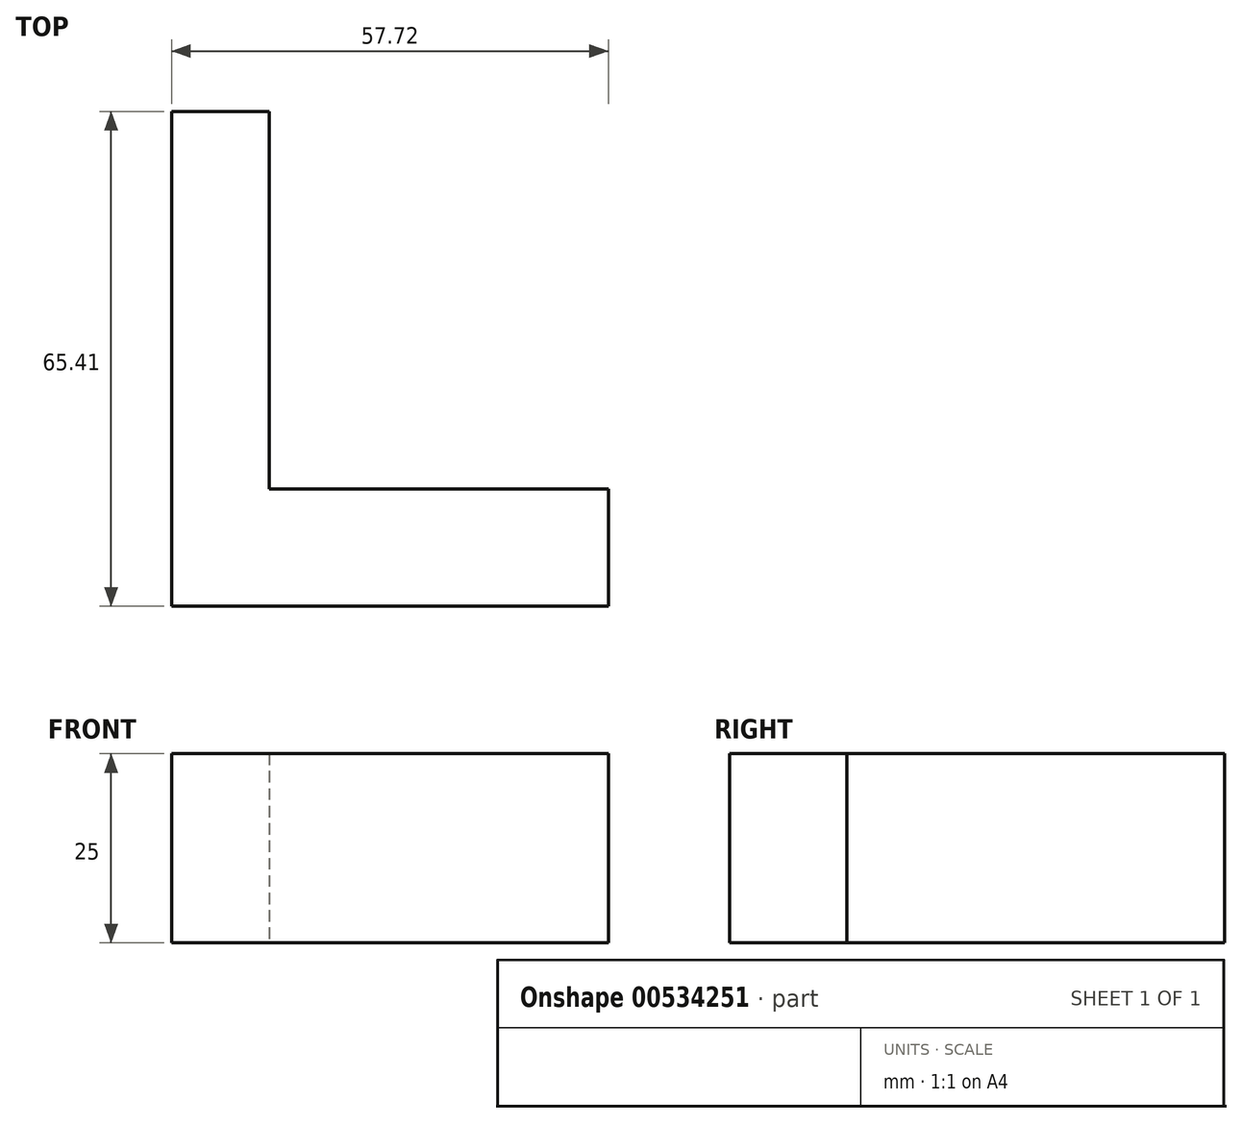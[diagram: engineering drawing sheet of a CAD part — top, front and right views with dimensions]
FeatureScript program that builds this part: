
annotation { "Feature Type Name" : "Feature", "Feature Type Description" : "" }
export const myFeature = defineFeature(function(context is Context, id is Id, definition is map)
    precondition{}
    {
        {
            var Q0;
            Q0=qCreatedBy(makeId("Top.planeOp"),FACE);
            var sketch = newSketch(context, id + "F0", { "sketchPlane" : qUnion([Q0])});
            skLineSegment(sketch, "E0", {"start": v(-23.84, 40.2) * mm, "end": v(-23.84, -25.2) * mm});
            skLineSegment(sketch, "E1", {"start": v(-23.84, -25.2) * mm, "end": v(33.88, -25.2) * mm});
            skLineSegment(sketch, "E2", {"start": v(33.88, -25.2) * mm, "end": v(33.88, -9.67) * mm});
            skLineSegment(sketch, "E3", {"start": v(33.88, -9.67) * mm, "end": v(-10.95, -9.67) * mm});
            skLineSegment(sketch, "E4", {"start": v(-10.95, -9.67) * mm, "end": v(-10.95, 40.2) * mm});
            skLineSegment(sketch, "E5", {"start": v(-10.95, 40.2) * mm, "end": v(-23.84, 40.2) * mm});
            skSolve(sketch);
        }
        {
            var Q0;
            Q0=makeQuery(id+"F0.imprint","IMPRINT",FACE,{"disambiguationData":[TD([[makeQuery(id+"F0.imprint","IMPRINT",EDGE,{"derivedFrom":sQuery(id+"F0.wireOp",EDGE,"nxsL3Kdy-C9Yg-rP7m-vsOs-Uaon2nxuVluv.bottom")}),-1.0]])]});
            var Q1;
            Q1=makeQuery(id+"F0.imprint","IMPRINT",FACE,{"disambiguationData":[TD([[makeQuery(id+"F0.imprint","IMPRINT",EDGE,{"derivedFrom":sQuery(id+"F0.wireOp",EDGE,"E0")}),1.0]])]});
            extrude(context, id + "F1", {"entities" : qUnion([Q0, Q1]), "depth" : 25 * mm, "offsetDistance" : 25 * mm});
        }
    });
